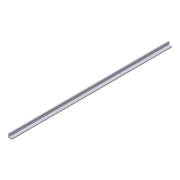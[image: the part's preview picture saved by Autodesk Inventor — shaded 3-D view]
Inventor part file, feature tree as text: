
AUTODESK INVENTOR PART (.ipt)
format: ipt  version: 2012 (Build 160160000, 160)  size: 63,488 bytes
history: native  units: in
note: dims shown in document units (in); Inventor stores cm internally (conversion verified against a paired STEP export)
features: extrude x1, sketch x1
ambient origin geometry x8: Origin, YZ Plane, XZ Plane, XY Plane, X Axis, Y Axis, Z Axis, Center Point
bodies: Solid1 (feature_tree)
feature tree (2):
  extrude  "Extrusion1"  Depth=1.0in
  sketch  "Sketch1"  dims[d0=1.0in d1=1.0in d2=0.25in d3=42.0in d4=0.0in]
